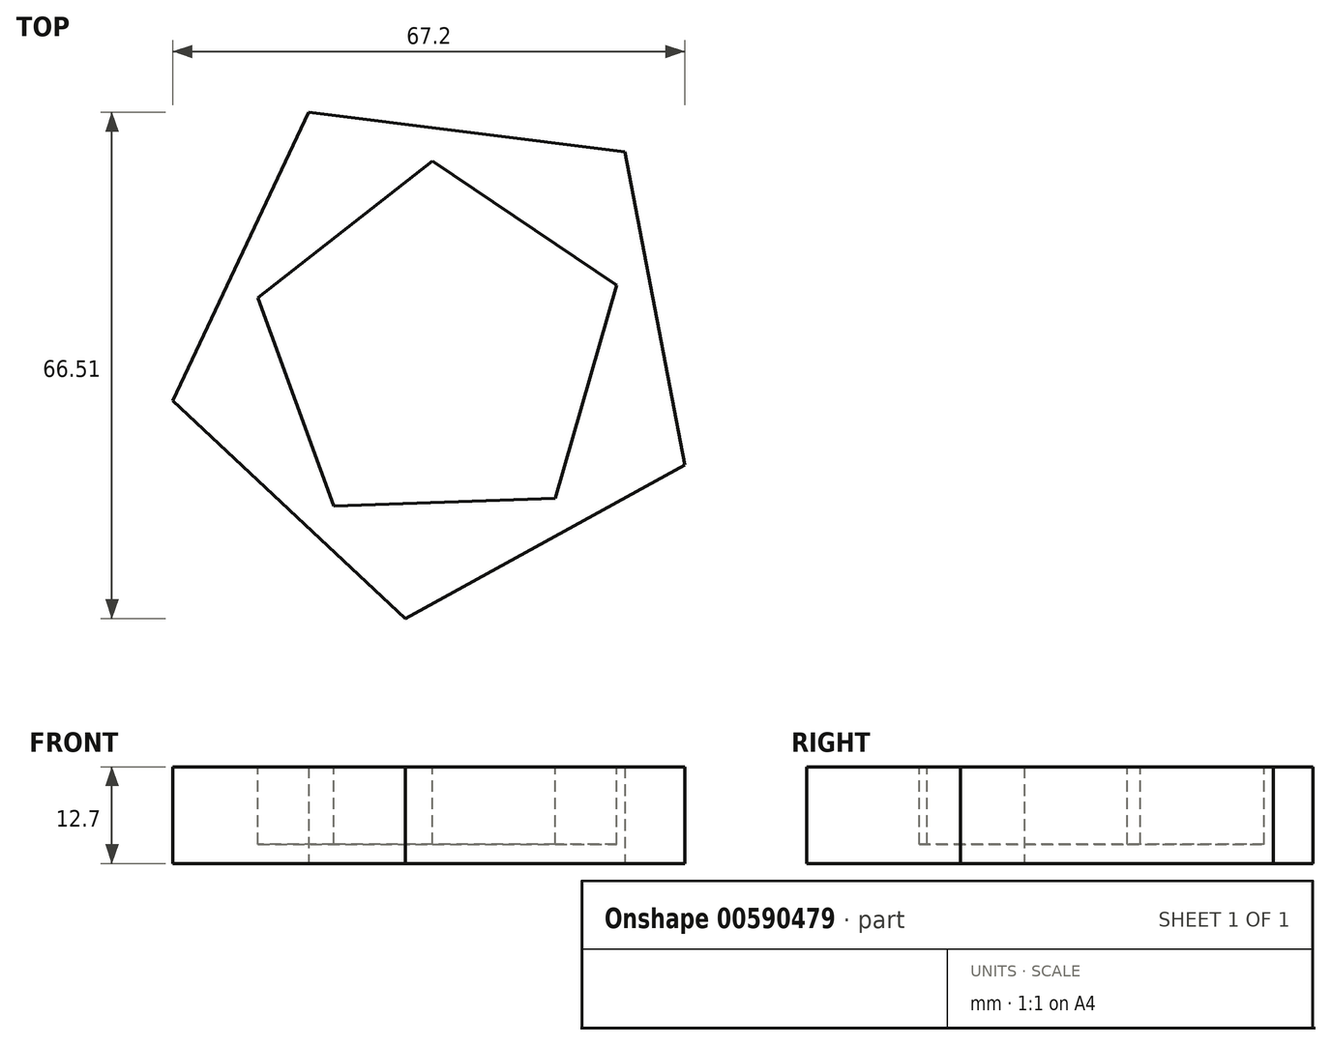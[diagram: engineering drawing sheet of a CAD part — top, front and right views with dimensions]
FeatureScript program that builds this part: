
annotation { "Feature Type Name" : "Feature", "Feature Type Description" : "" }
export const myFeature = defineFeature(function(context is Context, id is Id, definition is map)
    precondition{}
    {
        {
            var Q0;
            Q0=qCreatedBy(makeId("Top.planeOp"),FACE);
            var sketch = newSketch(context, id + "F0", { "sketchPlane" : qUnion([Q0])});
            skCircle(sketch, "E0.cCircle", {"center": v(0, 0) * mm, "radius": 28.8 * mm, "construction": true});
            skLineSegment(sketch, "E0.0", {"start": v(32.23, -15.13) * mm, "end": v(-4.43, -35.33) * mm});
            skLineSegment(sketch, "E0.1", {"start": v(-4.43, -35.33) * mm, "end": v(-34.97, -6.7) * mm});
            skLineSegment(sketch, "E0.2", {"start": v(-34.97, -6.7) * mm, "end": v(-17.18, 31.18) * mm});
            skLineSegment(sketch, "E0.3", {"start": v(-17.18, 31.18) * mm, "end": v(24.35, 25.98) * mm});
            skLineSegment(sketch, "E0.4", {"start": v(24.35, 25.98) * mm, "end": v(32.23, -15.13) * mm});
            skPoint(sketch, "E0.0.midPoint", {"position": v(13.9, -25.23) * mm});
            skSolve(sketch);
        }
        {
            var Q0;
            Q0 = qSketchRegion(id + "F0", true);
            extrude(context, id + "F1", {"entities" : qUnion([Q0]), "depth" : 12.7 * mm, "offsetDistance" : 25.4 * mm});
        }
        {
            var Q0;
            Q0=makeQuery(id+"F1.opExtrude","CAP_FACE",FACE,{"disambiguationData":[OSD([sQuery(id+"F0.wireOp",EDGE,"E0.0"),sQuery(id+"F0.wireOp",EDGE,"E0.1"),sQuery(id+"F0.wireOp",EDGE,"E0.2"),sQuery(id+"F0.wireOp",EDGE,"E0.3"),sQuery(id+"F0.wireOp",EDGE,"E0.4")])],"isStart":false});
            var sketch = newSketch(context, id + "F2", { "sketchPlane" : qUnion([Q0])});
            skCircle(sketch, "E1.cCircle", {"center": v(0, 0) * mm, "radius": 20.04 * mm, "construction": true});
            skLineSegment(sketch, "E1.0", {"start": v(23.28, 8.48) * mm, "end": v(15.25, -19.52) * mm});
            skLineSegment(sketch, "E1.1", {"start": v(15.25, -19.52) * mm, "end": v(-13.85, -20.54) * mm});
            skLineSegment(sketch, "E1.2", {"start": v(-13.85, -20.54) * mm, "end": v(-23.81, 6.83) * mm});
            skLineSegment(sketch, "E1.3", {"start": v(-23.81, 6.83) * mm, "end": v(-0.87, 24.76) * mm});
            skLineSegment(sketch, "E1.4", {"start": v(-0.87, 24.76) * mm, "end": v(23.28, 8.48) * mm});
            skPoint(sketch, "E1.0.midPoint", {"position": v(19.27, -5.52) * mm});
            skSolve(sketch);
        }
        {
            var Q0;
            Q0=makeQuery(id+"F2.imprint","IMPRINT",FACE,{"disambiguationData":[TD([[makeQuery(id+"F2.imprint","IMPRINT",EDGE,{"derivedFrom":sQuery(id+"F2.wireOp",EDGE,"E1.0")}),-1.0]])]});
            extrude(context, id + "F3", {"entities" : qUnion([Q0]), "operationType" : NewBodyOperationType.REMOVE, "oppositeDirection" : true, "depth" : 10.16 * mm, "offsetDistance" : 25.4 * mm});
        }
    });
